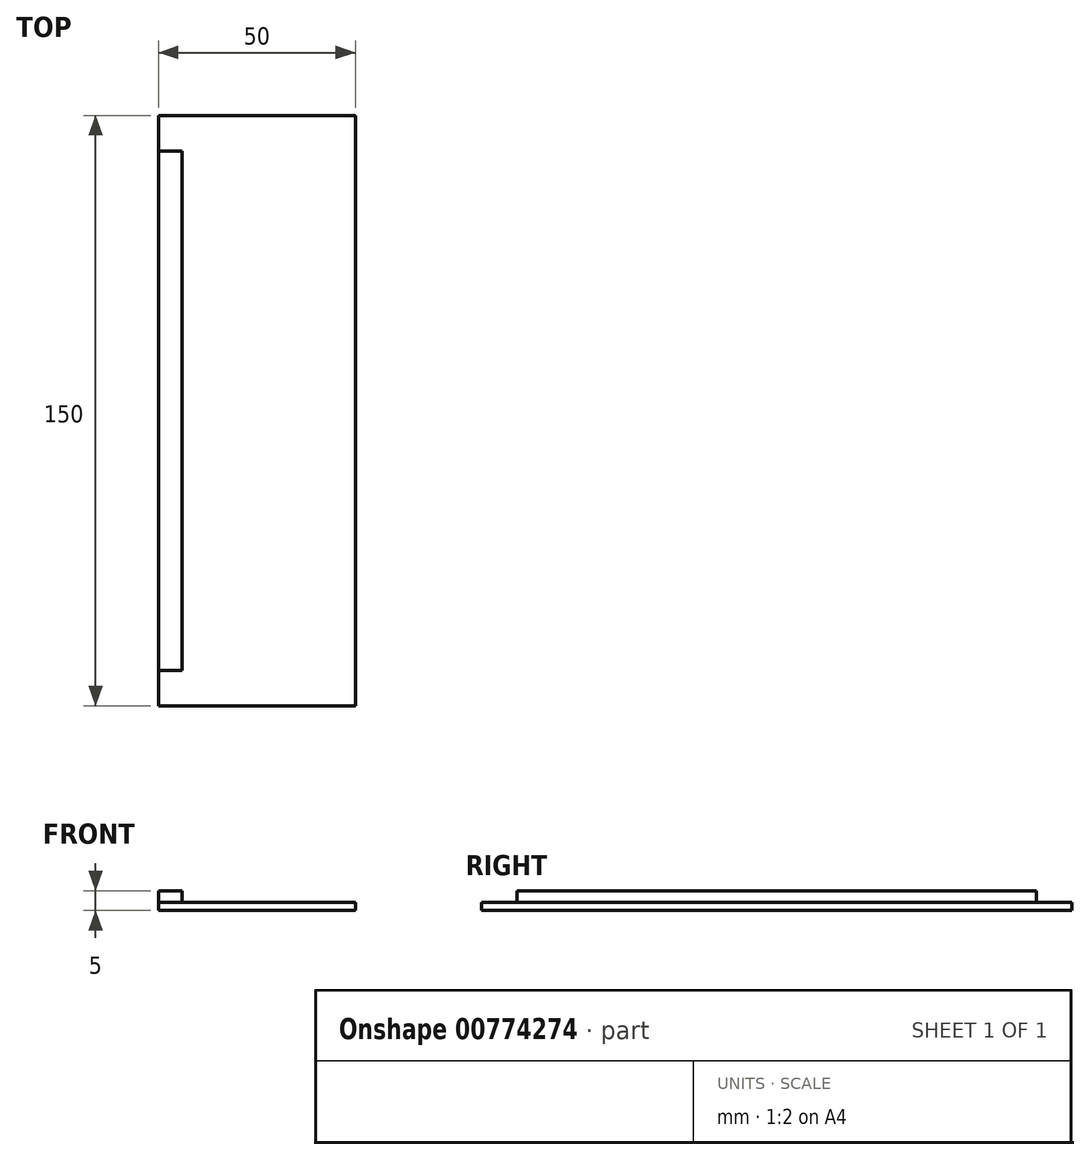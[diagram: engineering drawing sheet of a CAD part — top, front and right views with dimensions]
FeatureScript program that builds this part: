
annotation { "Feature Type Name" : "Feature", "Feature Type Description" : "" }
export const myFeature = defineFeature(function(context is Context, id is Id, definition is map)
    precondition{}
    {
        {
            var Q0;
            Q0=qCreatedBy(makeId("Top.planeOp"),FACE);
            var sketch = newSketch(context, id + "F0", { "sketchPlane" : qUnion([Q0])});
            skLineSegment(sketch, "E0.bottom", {"start": v(25, 75) * mm, "end": v(-25, 75) * mm});
            skLineSegment(sketch, "E0.top", {"start": v(25, -75) * mm, "end": v(-25, -75) * mm});
            skLineSegment(sketch, "E0.left", {"start": v(25, 75) * mm, "end": v(25, -75) * mm});
            skLineSegment(sketch, "E0.right", {"start": v(-25, 75) * mm, "end": v(-25, -75) * mm});
            skPoint(sketch, "E0.middle", {"position": v(0, 0) * mm});
            skSolve(sketch);
        }
        {
            var Q0;
            Q0 = qSketchRegion(id + "F0", true);
            extrude(context, id + "F1", {"entities" : qUnion([Q0]), "depth" : 2 * mm, "offsetDistance" : 25 * mm});
        }
        {
            var Q0;
            Q0=makeQuery(id+"F1.opExtrude","CAP_FACE",FACE,{"disambiguationData":[OSD([sQuery(id+"F0.wireOp",EDGE,"E0.bottom"),sQuery(id+"F0.wireOp",EDGE,"E0.top"),sQuery(id+"F0.wireOp",EDGE,"E0.left"),sQuery(id+"F0.wireOp",EDGE,"E0.right")])],"isStart":false});
            var sketch = newSketch(context, id + "F2", { "sketchPlane" : qUnion([Q0])});
            skLineSegment(sketch, "E1.bottom", {"start": v(-19, -66) * mm, "end": v(-31, -66) * mm});
            skLineSegment(sketch, "E1.top", {"start": v(-19, 66) * mm, "end": v(-31, 66) * mm});
            skLineSegment(sketch, "E1.left", {"start": v(-19, -66) * mm, "end": v(-19, 66) * mm});
            skLineSegment(sketch, "E1.right", {"start": v(-31, -66) * mm, "end": v(-31, 66) * mm});
            skPoint(sketch, "E1.middle", {"position": v(-25, 0) * mm});
            skSolve(sketch);
        }
        {
            var Q0;
            {var subQ0=sQuery(id+"F2.wireOp",EDGE,"E1.left");Q0=makeQuery(id+"F2.imprint","IMPRINT",FACE,{"disambiguationData":[TD([[makeQuery(id+"F2.imprint","IMPRINT",EDGE,{"derivedFrom":subQ0}),1.0]])]});}
            extrude(context, id + "F3", {"entities" : qUnion([Q0]), "operationType" : NewBodyOperationType.ADD, "depth" : 3 * mm, "offsetDistance" : 25 * mm});
        }
    });
